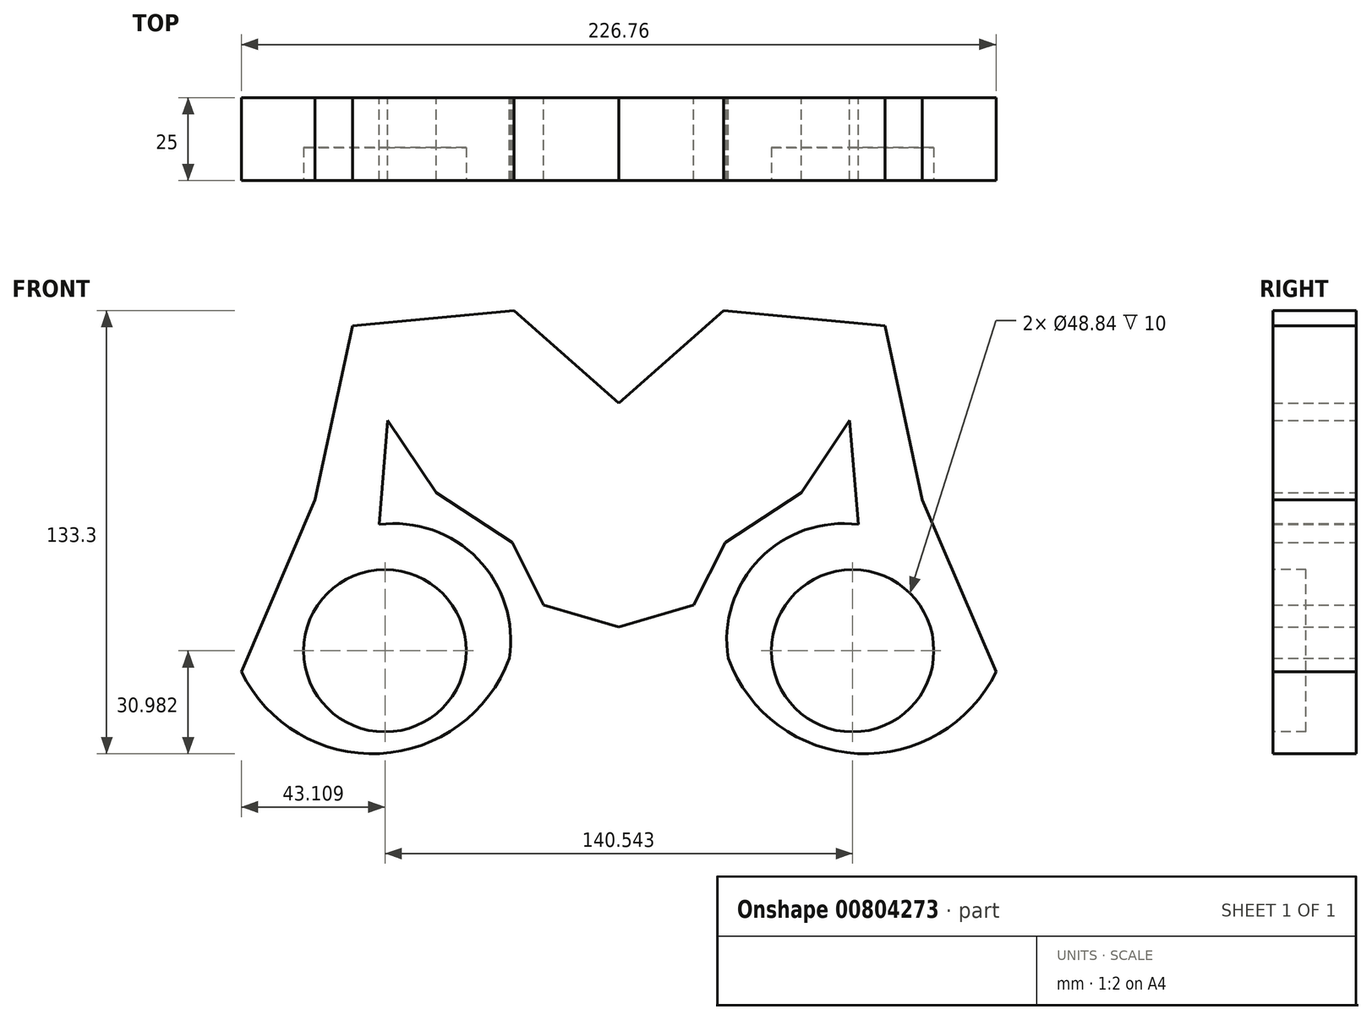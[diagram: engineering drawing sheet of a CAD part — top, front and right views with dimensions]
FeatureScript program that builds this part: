
annotation { "Feature Type Name" : "Feature", "Feature Type Description" : "" }
export const myFeature = defineFeature(function(context is Context, id is Id, definition is map)
    precondition{}
    {
        {
            var Q0;
            Q0=qCreatedBy(makeId("Front.planeOp"),FACE);
            var sketch = newSketch(context, id + "F0", { "sketchPlane" : qUnion([Q0])});
            skLineSegment(sketch, "E0", {"start": v(0, -40.38) * mm, "end": v(0, 49.3) * mm, "construction": true});
            skLineSegment(sketch, "E1", {"start": v(0, 33.77) * mm, "end": v(31.47, 61.65) * mm});
            skLineSegment(sketch, "E2", {"start": v(31.47, 61.65) * mm, "end": v(80.04, 57.05) * mm});
            skLineSegment(sketch, "E3", {"start": v(80.04, 57.05) * mm, "end": v(91.25, 4.74) * mm});
            skLineSegment(sketch, "E4", {"start": v(91.25, 4.74) * mm, "end": v(113.38, -47) * mm});
            skArc(sketch, "E5", {"start": v(32.9, -42.97) * mm, "mid": v(71.81, -71.6) * mm, "end": v(113.38, -47) * mm});
            skArc(sketch, "E6", {"start": v(72, -2.73) * mm, "mid": v(42.35, -13.04) * mm, "end": v(32.9, -42.97) * mm});
            skLineSegment(sketch, "E7", {"start": v(72, -2.73) * mm, "end": v(69.4, 28.6) * mm});
            skLineSegment(sketch, "E8", {"start": v(69.4, 28.6) * mm, "end": v(54.9, 6.84) * mm});
            skLineSegment(sketch, "E9", {"start": v(54.9, 6.84) * mm, "end": v(32.05, -8.2) * mm});
            skLineSegment(sketch, "E10", {"start": v(32.05, -8.2) * mm, "end": v(22.56, -26.87) * mm});
            skLineSegment(sketch, "E11", {"start": v(22.56, -26.87) * mm, "end": v(0, -33.48) * mm});
            skLineSegment(sketch, "E12.MirrorCS", {"start": v(0, 33.77) * mm, "end": v(-31.47, 61.65) * mm});
            skLineSegment(sketch, "E13.MirrorCS", {"start": v(-31.47, 61.65) * mm, "end": v(-80.04, 57.05) * mm});
            skLineSegment(sketch, "E14.MirrorCS", {"start": v(-80.04, 57.05) * mm, "end": v(-91.25, 4.74) * mm});
            skLineSegment(sketch, "E15.MirrorCS", {"start": v(-91.25, 4.74) * mm, "end": v(-113.38, -47) * mm});
            skArc(sketch, "E16.MirrorCS", {"start": v(-32.9, -42.97) * mm, "mid": v(-71.81, -71.6) * mm, "end": v(-113.38, -47) * mm});
            skArc(sketch, "E17.MirrorCS", {"start": v(-72, -2.73) * mm, "mid": v(-42.35, -13.04) * mm, "end": v(-32.9, -42.97) * mm});
            skLineSegment(sketch, "E18.MirrorCS", {"start": v(-72, -2.73) * mm, "end": v(-69.4, 28.6) * mm});
            skLineSegment(sketch, "E19.MirrorCS", {"start": v(-69.4, 28.6) * mm, "end": v(-54.9, 6.84) * mm});
            skLineSegment(sketch, "E20.MirrorCS", {"start": v(-54.9, 6.84) * mm, "end": v(-32.05, -8.2) * mm});
            skLineSegment(sketch, "E21.MirrorCS", {"start": v(-32.05, -8.2) * mm, "end": v(-22.56, -26.87) * mm});
            skLineSegment(sketch, "E22.MirrorCS", {"start": v(-22.56, -26.87) * mm, "end": v(0, -33.48) * mm});
            skSolve(sketch);
        }
        {
            var Q0;
            Q0 = qSketchRegion(id + "F0", true);
            extrude(context, id + "F1", {"entities" : qUnion([Q0]), "depth" : 25 * mm, "offsetDistance" : 25 * mm});
        }
        {
            var Q0;
            Q0=makeQuery(id+"F1.opExtrude","CAP_FACE",FACE,{"disambiguationData":[OSD([sQuery(id+"F0.wireOp",EDGE,"E1"),sQuery(id+"F0.wireOp",EDGE,"E2"),sQuery(id+"F0.wireOp",EDGE,"E3"),sQuery(id+"F0.wireOp",EDGE,"E4"),sQuery(id+"F0.wireOp",EDGE,"E5"),sQuery(id+"F0.wireOp",EDGE,"E6"),sQuery(id+"F0.wireOp",EDGE,"E7"),sQuery(id+"F0.wireOp",EDGE,"E8"),sQuery(id+"F0.wireOp",EDGE,"E9"),sQuery(id+"F0.wireOp",EDGE,"E10"),sQuery(id+"F0.wireOp",EDGE,"E11"),sQuery(id+"F0.wireOp",EDGE,"E12.MirrorCS"),sQuery(id+"F0.wireOp",EDGE,"E13.MirrorCS"),sQuery(id+"F0.wireOp",EDGE,"E14.MirrorCS"),sQuery(id+"F0.wireOp",EDGE,"E15.MirrorCS"),sQuery(id+"F0.wireOp",EDGE,"E16.MirrorCS"),sQuery(id+"F0.wireOp",EDGE,"E17.MirrorCS"),sQuery(id+"F0.wireOp",EDGE,"E18.MirrorCS"),sQuery(id+"F0.wireOp",EDGE,"E19.MirrorCS"),sQuery(id+"F0.wireOp",EDGE,"E20.MirrorCS"),sQuery(id+"F0.wireOp",EDGE,"E21.MirrorCS"),sQuery(id+"F0.wireOp",EDGE,"E22.MirrorCS")])],"isStart":false});
            var sketch = newSketch(context, id + "F2", { "sketchPlane" : qUnion([Q0])});
            skCircle(sketch, "E23", {"center": v(-70.27, -40.67) * mm, "radius": 24.42 * mm});
            skCircle(sketch, "E24.MirrorC", {"center": v(70.27, -40.67) * mm, "radius": 24.42 * mm});
            skSolve(sketch);
        }
        {
            var Q0;
            Q0 = qSketchRegion(id + "F2", true);
            extrude(context, id + "F3", {"entities" : qUnion([Q0]), "operationType" : NewBodyOperationType.REMOVE, "oppositeDirection" : true, "depth" : 10 * mm, "offsetDistance" : 25 * mm});
        }
    });
